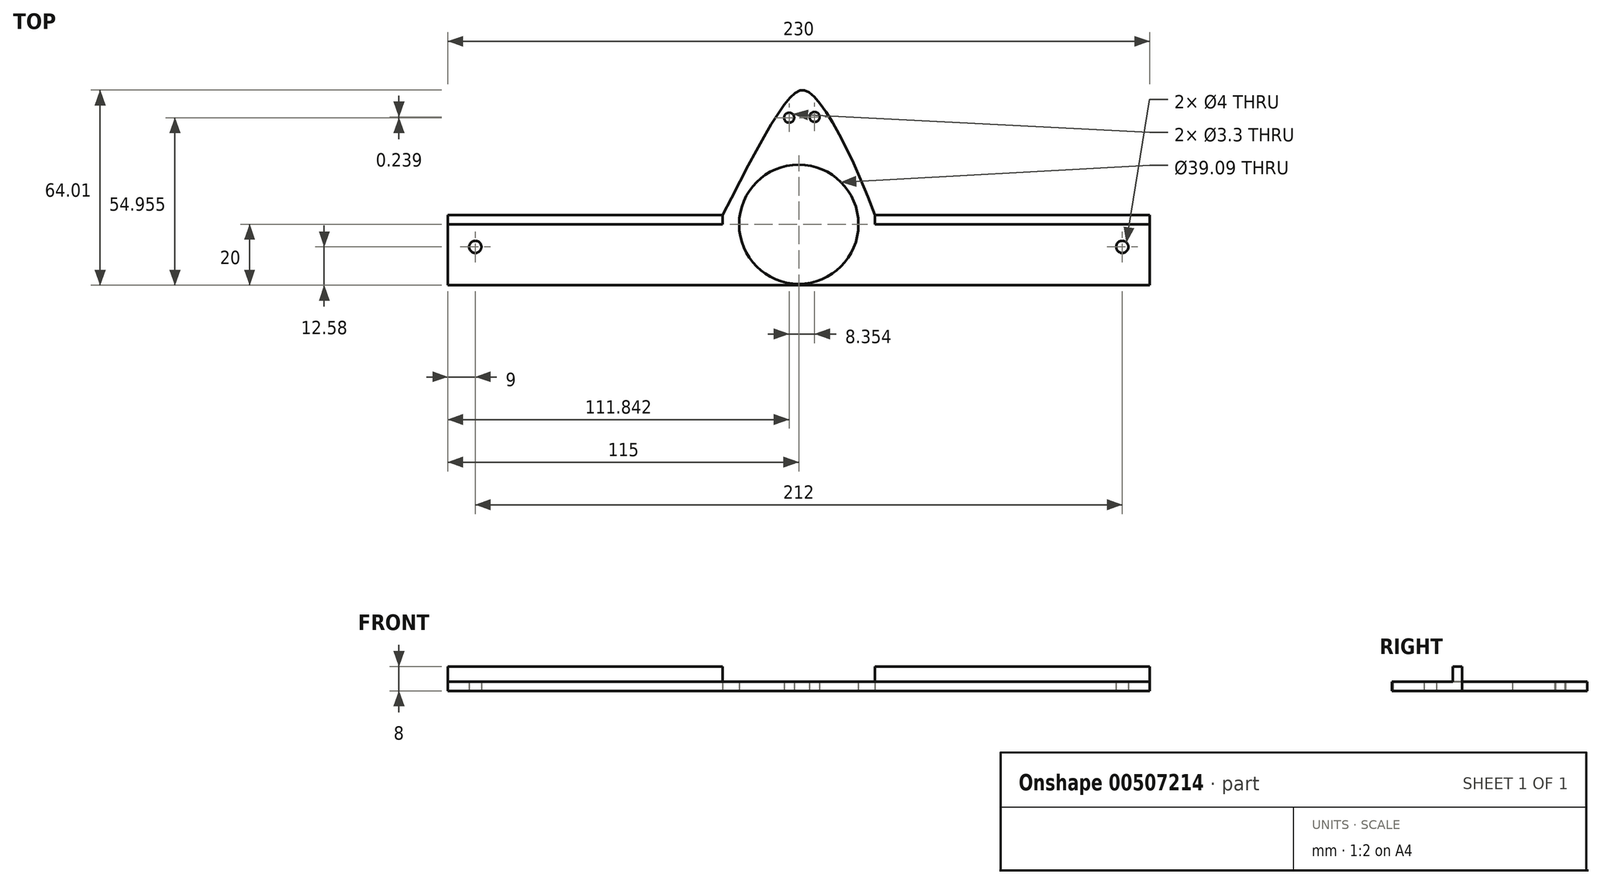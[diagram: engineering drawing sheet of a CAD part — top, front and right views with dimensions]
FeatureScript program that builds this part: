
annotation { "Feature Type Name" : "Feature", "Feature Type Description" : "" }
export const myFeature = defineFeature(function(context is Context, id is Id, definition is map)
    precondition{}
    {
        {
            var Q0;
            Q0=qCreatedBy(makeId("Top.planeOp"),FACE);
            var sketch = newSketch(context, id + "F0", { "sketchPlane" : qUnion([Q0])});
            skLineSegment(sketch, "E0.bottom", {"start": v(-115, 10) * mm, "end": v(115, 10) * mm});
            skLineSegment(sketch, "E0.top", {"start": v(-115, -10) * mm, "end": v(115, -10) * mm});
            skLineSegment(sketch, "E0.left", {"start": v(-115, 10) * mm, "end": v(-115, -10) * mm});
            skLineSegment(sketch, "E0.right", {"start": v(115, 10) * mm, "end": v(115, -10) * mm});
            skPoint(sketch, "E0.middle", {"position": v(0, 0) * mm});
            skLineSegment(sketch, "E1.top", {"start": v(-115, 13) * mm, "end": v(115, 13) * mm});
            skLineSegment(sketch, "E1.left", {"start": v(-115, 10) * mm, "end": v(-115, 13) * mm});
            skLineSegment(sketch, "E1.right", {"start": v(115, 10) * mm, "end": v(115, 13) * mm});
            skFitSpline(sketch, "E2", {"points": [v(-25, 13) * mm, v(-1.26, 53) * mm, v(3.74, 53) * mm, v(25, 13) * mm], "startDerivative": vector(67.85, 130.48) * mm, "endDerivative": vector(53.58, -141.55) * mm});
            skPoint(sketch, "E3", {"position": v(-25, 10) * mm});
            skPoint(sketch, "E4", {"position": v(25, 10) * mm});
            skLineSegment(sketch, "E5", {"start": v(25, 10) * mm, "end": v(25, 13) * mm});
            skLineSegment(sketch, "E6", {"start": v(-25, 13) * mm, "end": v(-25, 10) * mm});
            skCircle(sketch, "E7", {"center": v(106, 2.58) * mm, "radius": 2 * mm});
            skCircle(sketch, "E8", {"center": v(-106, 2.58) * mm, "radius": 2 * mm});
            skCircle(sketch, "E9", {"center": v(0, 10) * mm, "radius": 19.55 * mm});
            skCircle(sketch, "E10", {"center": v(-3.16, 44.95) * mm, "radius": 1.65 * mm});
            skCircle(sketch, "E11", {"center": v(5.2, 45.2) * mm, "radius": 1.65 * mm});
            skSolve(sketch);
        }
        {
            var Q0;
            Q0=makeQuery(id+"F0.imprint","IMPRINT",FACE,{"disambiguationData":[TD([[makeQuery(id+"F0.imprint","IMPRINT",EDGE,{"derivedFrom":sQuery(id+"F0.wireOp",EDGE,"E0.top")}),1.0]])]});
            extrude(context, id + "F1", {"entities" : qUnion([Q0]), "depth" : 2 * mm});
        }
        {
            var Q0;
            {var subQ4=sQuery(id+"F0.wireOp",EDGE,"E1.left");Q0=makeQuery(id+"F0.imprint","IMPRINT",FACE,{"disambiguationData":[TD([[makeQuery(id+"F0.imprint","IMPRINT",EDGE,{"derivedFrom":subQ4}),-1.0]])]});}
            extrude(context, id + "F2", {"entities" : qUnion([Q0]), "operationType" : NewBodyOperationType.ADD, "depth" : 8 * mm, "offsetDistance" : 25 * mm});
        }
        {
            var Q0;
            Q0 = qSketchRegion(id + "F0", true);
            extrude(context, id + "F3", {"entities" : qUnion([Q0]), "operationType" : NewBodyOperationType.ADD, "depth" : 3 * mm, "offsetDistance" : 25 * mm});
        }
        {
            var Q0;
            {var subQ0=sQuery(id+"F0.wireOp",EDGE,"E1.right");Q0=makeQuery(id+"F0.imprint","IMPRINT",FACE,{"disambiguationData":[TD([[makeQuery(id+"F0.imprint","IMPRINT",EDGE,{"derivedFrom":subQ0}),1.0]])]});}
            extrude(context, id + "F4", {"entities" : qUnion([Q0]), "operationType" : NewBodyOperationType.ADD, "depth" : 8 * mm, "offsetDistance" : 25 * mm});
        }
    });
